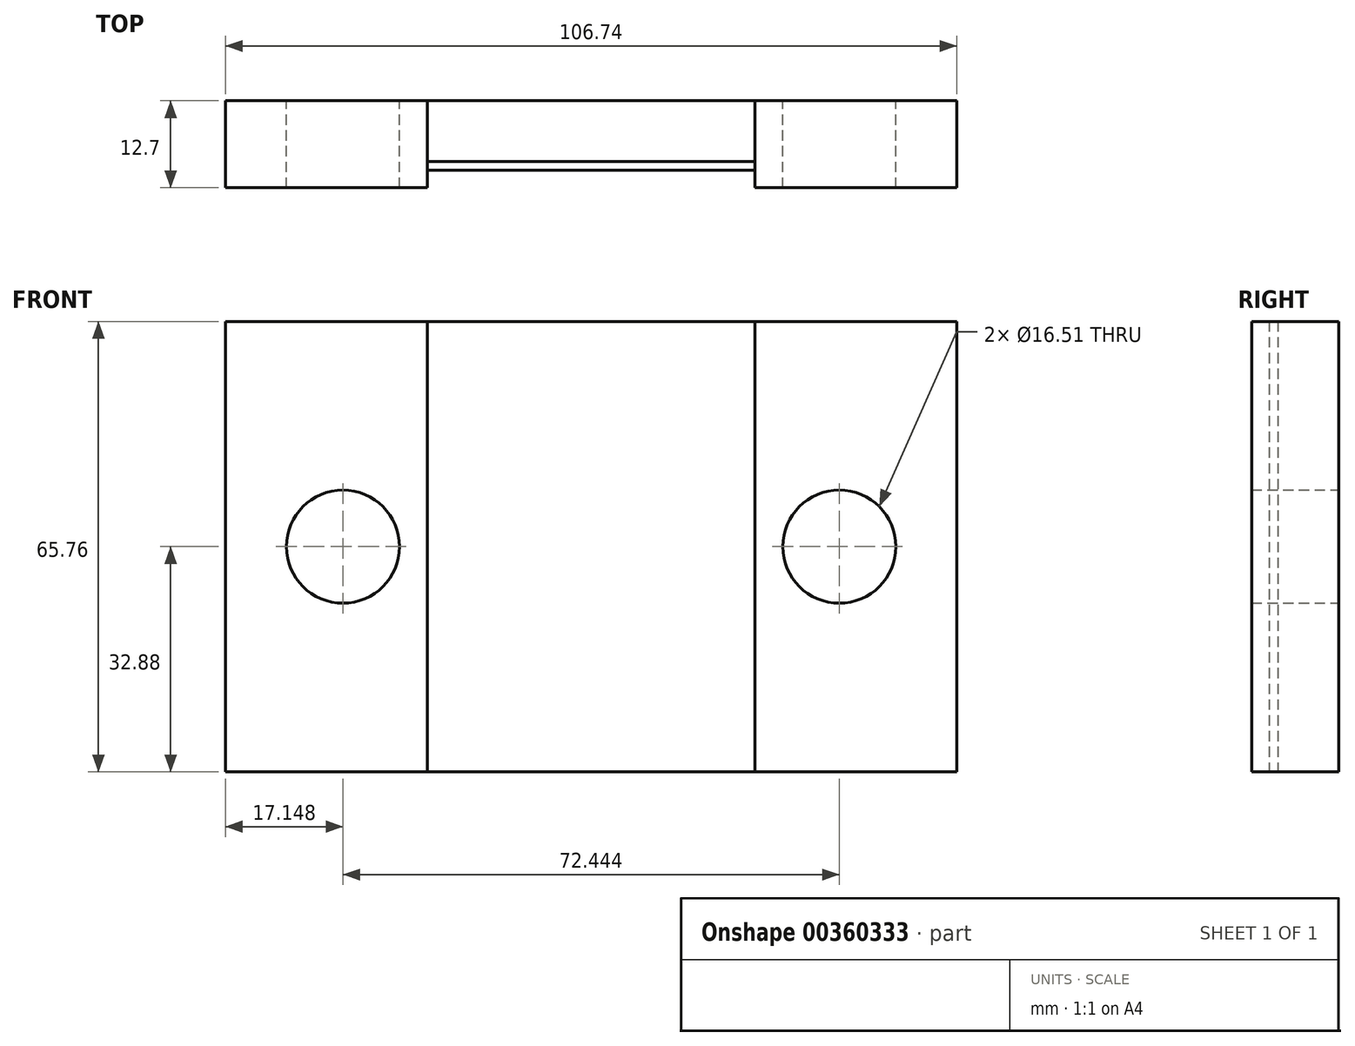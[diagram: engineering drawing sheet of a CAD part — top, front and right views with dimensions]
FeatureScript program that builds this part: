
annotation { "Feature Type Name" : "Feature", "Feature Type Description" : "" }
export const myFeature = defineFeature(function(context is Context, id is Id, definition is map)
    precondition{}
    {
        {
            var Q0;
            Q0=qCreatedBy(makeId("Front.planeOp"),FACE);
            var sketch = newSketch(context, id + "F0", { "sketchPlane" : qUnion([Q0])});
            skLineSegment(sketch, "E0.bottom", {"start": v(53.37, 32.88) * mm, "end": v(-53.37, 32.88) * mm});
            skLineSegment(sketch, "E0.top", {"start": v(53.37, -32.88) * mm, "end": v(-53.37, -32.88) * mm});
            skLineSegment(sketch, "E0.left", {"start": v(53.37, 32.88) * mm, "end": v(53.37, -32.88) * mm});
            skLineSegment(sketch, "E0.right", {"start": v(-53.37, 32.88) * mm, "end": v(-53.37, -32.88) * mm});
            skPoint(sketch, "E0.middle", {"position": v(0, 0) * mm});
            skCircle(sketch, "E1", {"center": v(-36.22, 0) * mm, "radius": 8.26 * mm});
            skCircle(sketch, "E2", {"center": v(36.22, 0) * mm, "radius": 8.26 * mm});
            skLineSegment(sketch, "E3", {"start": v(-23.89, 32.88) * mm, "end": v(-23.89, -32.88) * mm});
            skLineSegment(sketch, "E4", {"start": v(23.89, 32.88) * mm, "end": v(23.89, -32.88) * mm});
            skSolve(sketch);
        }
        {
            var Q0;
            Q0=makeQuery(id+"F0.imprint","IMPRINT",FACE,{"disambiguationData":[TD([[makeQuery(id+"F0.imprint","IMPRINT",EDGE,{"derivedFrom":sQuery(id+"F0.wireOp",EDGE,"E0.bottom")}),1.0]])]});
            extrude(context, id + "F1", {"entities" : qUnion([Q0]), "depth" : 10.16 * mm});
        }
        {
            var Q0;
            Q0=makeQuery(id+"F0.imprint","IMPRINT",FACE,{"disambiguationData":[TD([[makeQuery(id+"F0.imprint","IMPRINT",EDGE,{"derivedFrom":sQuery(id+"F0.wireOp",EDGE,"E0.bottom")}),1.0]])]});
            extrude(context, id + "F2", {"entities" : qUnion([Q0]), "depth" : 8.9 * mm});
        }
        {
            var Q0;
            {var subQ0=sQuery(id+"F0.wireOp",EDGE,"E0.right");Q0=makeQuery(id+"F0.imprint","IMPRINT",FACE,{"disambiguationData":[TD([[makeQuery(id+"F0.imprint","IMPRINT",EDGE,{"derivedFrom":subQ0}),1.0]])]});}
            var Q1;
            {var subQ0=sQuery(id+"F0.wireOp",EDGE,"E0.left");Q1=makeQuery(id+"F0.imprint","IMPRINT",FACE,{"disambiguationData":[TD([[makeQuery(id+"F0.imprint","IMPRINT",EDGE,{"derivedFrom":subQ0}),-1.0]])]});}
            extrude(context, id + "F3", {"entities" : qUnion([Q0, Q1]), "depth" : 12.7 * mm});
        }
    });
